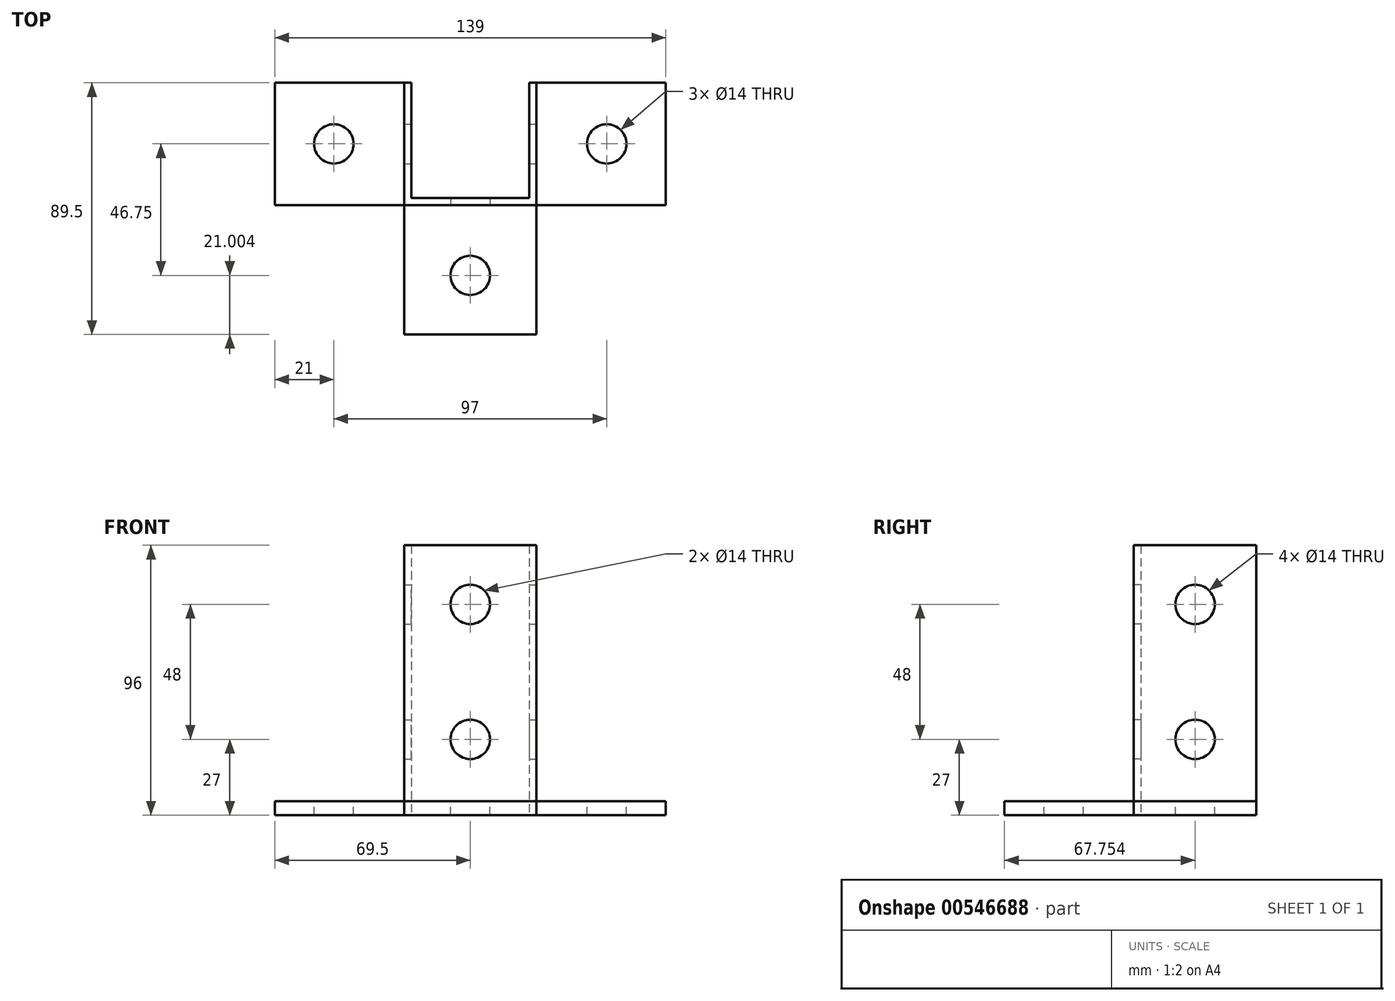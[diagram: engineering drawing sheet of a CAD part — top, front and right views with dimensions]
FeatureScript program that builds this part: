
annotation { "Feature Type Name" : "Feature", "Feature Type Description" : "" }
export const myFeature = defineFeature(function(context is Context, id is Id, definition is map)
    precondition{}
    {
        {
            var Q0;
            Q0=qCreatedBy(makeId("Top.planeOp"),FACE);
            var sketch = newSketch(context, id + "F0", { "sketchPlane" : qUnion([Q0])});
            skLineSegment(sketch, "E0", {"start": v(-21, 19.5) * mm, "end": v(-21, -21.5) * mm});
            skLineSegment(sketch, "E1", {"start": v(-21, -21.5) * mm, "end": v(21, -21.5) * mm});
            skLineSegment(sketch, "E2", {"start": v(21, -21.5) * mm, "end": v(21, 19.5) * mm});
            skLineSegment(sketch, "E3", {"start": v(-21, 19.5) * mm, "end": v(-23.5, 19.5) * mm});
            skLineSegment(sketch, "E4", {"start": v(-23.5, 19.5) * mm, "end": v(-23.5, -24) * mm});
            skLineSegment(sketch, "E5", {"start": v(-23.5, -24) * mm, "end": v(23.5, -24) * mm});
            skLineSegment(sketch, "E6", {"start": v(23.5, -24) * mm, "end": v(23.5, 19.5) * mm});
            skLineSegment(sketch, "E7", {"start": v(23.5, 19.5) * mm, "end": v(21, 19.5) * mm});
            skSolve(sketch);
        }
        {
            var Q0;
            Q0=makeQuery(id+"F0.imprint","IMPRINT",FACE,{"disambiguationData":[TD([[makeQuery(id+"F0.imprint","IMPRINT",EDGE,{"derivedFrom":sQuery(id+"F0.wireOp",EDGE,"E0")}),-1.0]])]});
            extrude(context, id + "F1", {"entities" : qUnion([Q0]), "depth" : 96 * mm, "offsetDistance" : 25 * mm});
        }
        {
            var Q0;
            Q0=makeQuery(id+"F1.opExtrude","SWEPT_FACE",FACE,{"disambiguationData":[OSD([sQuery(id+"F0.wireOp",EDGE,"E6")])]});
            var sketch = newSketch(context, id + "F2", { "sketchPlane" : qUnion([Q0])});
            skLineSegment(sketch, "E8.bottom", {"start": v(-24, 0) * mm, "end": v(19.5, 0) * mm});
            skLineSegment(sketch, "E8.top", {"start": v(-24, 5) * mm, "end": v(19.5, 5) * mm});
            skLineSegment(sketch, "E8.left", {"start": v(-24, 0) * mm, "end": v(-24, 5) * mm});
            skLineSegment(sketch, "E8.right", {"start": v(19.5, 0) * mm, "end": v(19.5, 5) * mm});
            skSolve(sketch);
        }
        {
            var Q0;
            Q0 = qSketchRegion(id + "F2", true);
            extrude(context, id + "F3", {"entities" : qUnion([Q0]), "operationType" : NewBodyOperationType.ADD, "depth" : 46 * mm, "offsetDistance" : 25 * mm});
        }
        {
            var Q0;
            Q0=makeQuery(id+"F3.boolean.opBoolean","MERGE",FACE,{"derivedFrom":[makeQuery(id+"F1.opExtrude","SWEPT_FACE",FACE,{"disambiguationData":[OSD([sQuery(id+"F0.wireOp",EDGE,"E5")])]}),makeQuery(id+"F3.opExtrude","SWEPT_FACE",FACE,{"disambiguationData":[OSD([sQuery(id+"F2.wireOp",EDGE,"E8.left")])]})]});
            var sketch = newSketch(context, id + "F4", { "sketchPlane" : qUnion([Q0])});
            skPoint(sketch, "E9.oppositeSnap0", {"position": v(23, 0) * mm});
            skLineSegment(sketch, "E9.bottom", {"start": v(-23.5, 5) * mm, "end": v(23.5, 5) * mm});
            skLineSegment(sketch, "E9.top", {"start": v(-23.5, 0) * mm, "end": v(23.5, 0) * mm});
            skLineSegment(sketch, "E9.left", {"start": v(-23.5, 5) * mm, "end": v(-23.5, 0) * mm});
            skLineSegment(sketch, "E9.right", {"start": v(23.5, 5) * mm, "end": v(23.5, 0) * mm});
            skSolve(sketch);
        }
        {
            var Q0;
            Q0=makeQuery(id+"F4.imprint","IMPRINT",FACE,{"disambiguationData":[TD([[makeQuery(id+"F4.imprint","IMPRINT",EDGE,{"derivedFrom":sQuery(id+"F4.wireOp",EDGE,"E9.bottom")}),-1.0]])]});
            extrude(context, id + "F5", {"entities" : qUnion([Q0]), "operationType" : NewBodyOperationType.ADD, "depth" : 46 * mm, "offsetDistance" : 25 * mm});
        }
        {
            var Q0;
            Q0=makeQuery(id+"F5.boolean.opBoolean","MERGE",FACE,{"derivedFrom":[makeQuery(id+"F1.opExtrude","SWEPT_FACE",FACE,{"disambiguationData":[OSD([sQuery(id+"F0.wireOp",EDGE,"E4")])]}),makeQuery(id+"F5.opExtrude","SWEPT_FACE",FACE,{"disambiguationData":[OSD([sQuery(id+"F4.wireOp",EDGE,"E9.left")])]})]});
            var sketch = newSketch(context, id + "F6", { "sketchPlane" : qUnion([Q0])});
            skLineSegment(sketch, "E10.bottom", {"start": v(-19.5, 0) * mm, "end": v(24, 0) * mm});
            skLineSegment(sketch, "E10.top", {"start": v(-19.5, 5) * mm, "end": v(24, 5) * mm});
            skLineSegment(sketch, "E10.left", {"start": v(-19.5, 0) * mm, "end": v(-19.5, 5) * mm});
            skLineSegment(sketch, "E10.right", {"start": v(24, 0) * mm, "end": v(24, 5) * mm});
            skSolve(sketch);
        }
        {
            var Q0;
            Q0=makeQuery(id+"F6.imprint","IMPRINT",FACE,{"disambiguationData":[TD([[makeQuery(id+"F6.imprint","IMPRINT",EDGE,{"derivedFrom":sQuery(id+"F6.wireOp",EDGE,"E10.bottom")}),1.0]])]});
            extrude(context, id + "F7", {"entities" : qUnion([Q0]), "operationType" : NewBodyOperationType.ADD, "depth" : 46 * mm, "offsetDistance" : 25 * mm});
        }
        {
            var Q0;
            Q0=makeQuery(id+"F7.opExtrude","SWEPT_FACE",FACE,{"disambiguationData":[OSD([sQuery(id+"F6.wireOp",EDGE,"E10.top")])]});
            var sketch = newSketch(context, id + "F8", { "sketchPlane" : qUnion([Q0])});
            skCircle(sketch, "E11", {"center": v(-48.5, -2.26) * mm, "radius": 3.53 * mm});
            skCircle(sketch, "E12", {"center": v(48.5, -2.26) * mm, "radius": 5.09 * mm});
            skCircle(sketch, "E13", {"center": v(0, -49) * mm, "radius": 5.46 * mm});
            skSolve(sketch);
        }
        {
            var Q0;
            Q0=sQuery(id+"F8.wireOp",VERTEX,"E11.center");
            var Q1;
            Q1=sQuery(id+"F8.wireOp",VERTEX,"E13.center");
            var Q2;
            Q2=sQuery(id+"F8.wireOp",VERTEX,"E12.center");
            var Q3;
            Q3=makeQuery(id+"F1.opExtrude","SWEPT_BODY",BODY,{"disambiguationData":[OSD([sQuery(id+"F0.wireOp",EDGE,"E0"),sQuery(id+"F0.wireOp",EDGE,"E1"),sQuery(id+"F0.wireOp",EDGE,"E2"),sQuery(id+"F0.wireOp",EDGE,"E3"),sQuery(id+"F0.wireOp",EDGE,"E4"),sQuery(id+"F0.wireOp",EDGE,"E5"),sQuery(id+"F0.wireOp",EDGE,"E6"),sQuery(id+"F0.wireOp",EDGE,"E7")])]});
            hole(context, id + "F9", {"style" : HoleStyle.SIMPLE, "endStyle" : HoleEndStyle.THROUGH, "holeDiameter" : 14 * mm, "tappedDepth" : 12 * mm, "tapClearance" : 3, "locations" : qUnion([Q0, Q1, Q2]), "scope" : qUnion([Q3])});
        }
        {
            var Q0;
            {var subQ1=sQuery(id+"F0.wireOp",EDGE,"E4");var subQ2=sQuery(id+"F0.wireOp",EDGE,"E5");var subQ3=makeQuery(id+"F1.opExtrude","SWEPT_FACE",FACE,{"disambiguationData":[OSD([subQ2])]});var subQ4=makeQuery(id+"F3.opExtrude","SWEPT_FACE",FACE,{"disambiguationData":[OSD([sQuery(id+"F2.wireOp",EDGE,"E8.left")])]});Q0=makeQuery(id+"F5.boolean.opBoolean","SPLIT",FACE,{"disambiguationData":[TD([makeQuery(id+"F1.opExtrude","SWEPT_FACE",FACE,{"disambiguationData":[OSD([subQ1])]})])],"derivedFrom":makeQuery(id+"F3.boolean.opBoolean","MERGE",FACE,{"derivedFrom":[subQ3,subQ4]})});}
            var sketch = newSketch(context, id + "F10", { "sketchPlane" : qUnion([Q0])});
            skCircle(sketch, "E14", {"center": v(0, 75) * mm, "radius": 5.56 * mm});
            skCircle(sketch, "E15", {"center": v(0, 27) * mm, "radius": 6.64 * mm});
            skSolve(sketch);
        }
        {
            var Q0;
            Q0=sQuery(id+"F10.wireOp",VERTEX,"E14.center");
            var Q1;
            Q1=sQuery(id+"F10.wireOp",VERTEX,"E15.center");
            var Q2;
            Q2=makeQuery(id+"F1.opExtrude","SWEPT_BODY",BODY,{"disambiguationData":[OSD([sQuery(id+"F0.wireOp",EDGE,"E0"),sQuery(id+"F0.wireOp",EDGE,"E1"),sQuery(id+"F0.wireOp",EDGE,"E2"),sQuery(id+"F0.wireOp",EDGE,"E3"),sQuery(id+"F0.wireOp",EDGE,"E4"),sQuery(id+"F0.wireOp",EDGE,"E5"),sQuery(id+"F0.wireOp",EDGE,"E6"),sQuery(id+"F0.wireOp",EDGE,"E7")])]});
            hole(context, id + "F11", {"style" : HoleStyle.SIMPLE, "endStyle" : HoleEndStyle.THROUGH, "holeDiameter" : 14 * mm, "tappedDepth" : 12 * mm, "tapClearance" : 3, "locations" : qUnion([Q0, Q1]), "scope" : qUnion([Q2])});
        }
        {
            var Q0;
            Q0=makeQuery(id+"F1.opExtrude","SWEPT_FACE",FACE,{"disambiguationData":[OSD([sQuery(id+"F0.wireOp",EDGE,"E6")])]});
            var sketch = newSketch(context, id + "F12", { "sketchPlane" : qUnion([Q0])});
            skCircle(sketch, "E16", {"center": v(-2.26, 75) * mm, "radius": 5.15 * mm});
            skCircle(sketch, "E17", {"center": v(-2.26, 27) * mm, "radius": 6.64 * mm});
            skSolve(sketch);
        }
        {
            var Q0;
            Q0=sQuery(id+"F12.wireOp",VERTEX,"E16.center");
            var Q1;
            Q1=sQuery(id+"F12.wireOp",VERTEX,"E17.center");
            var Q2;
            Q2=makeQuery(id+"F1.opExtrude","SWEPT_BODY",BODY,{"disambiguationData":[OSD([sQuery(id+"F0.wireOp",EDGE,"E0"),sQuery(id+"F0.wireOp",EDGE,"E1"),sQuery(id+"F0.wireOp",EDGE,"E2"),sQuery(id+"F0.wireOp",EDGE,"E3"),sQuery(id+"F0.wireOp",EDGE,"E4"),sQuery(id+"F0.wireOp",EDGE,"E5"),sQuery(id+"F0.wireOp",EDGE,"E6"),sQuery(id+"F0.wireOp",EDGE,"E7")])]});
            hole(context, id + "F13", {"style" : HoleStyle.SIMPLE, "endStyle" : HoleEndStyle.THROUGH, "holeDiameter" : 14 * mm, "tappedDepth" : 12 * mm, "tapClearance" : 3, "locations" : qUnion([Q0, Q1]), "scope" : qUnion([Q2])});
        }
    });
